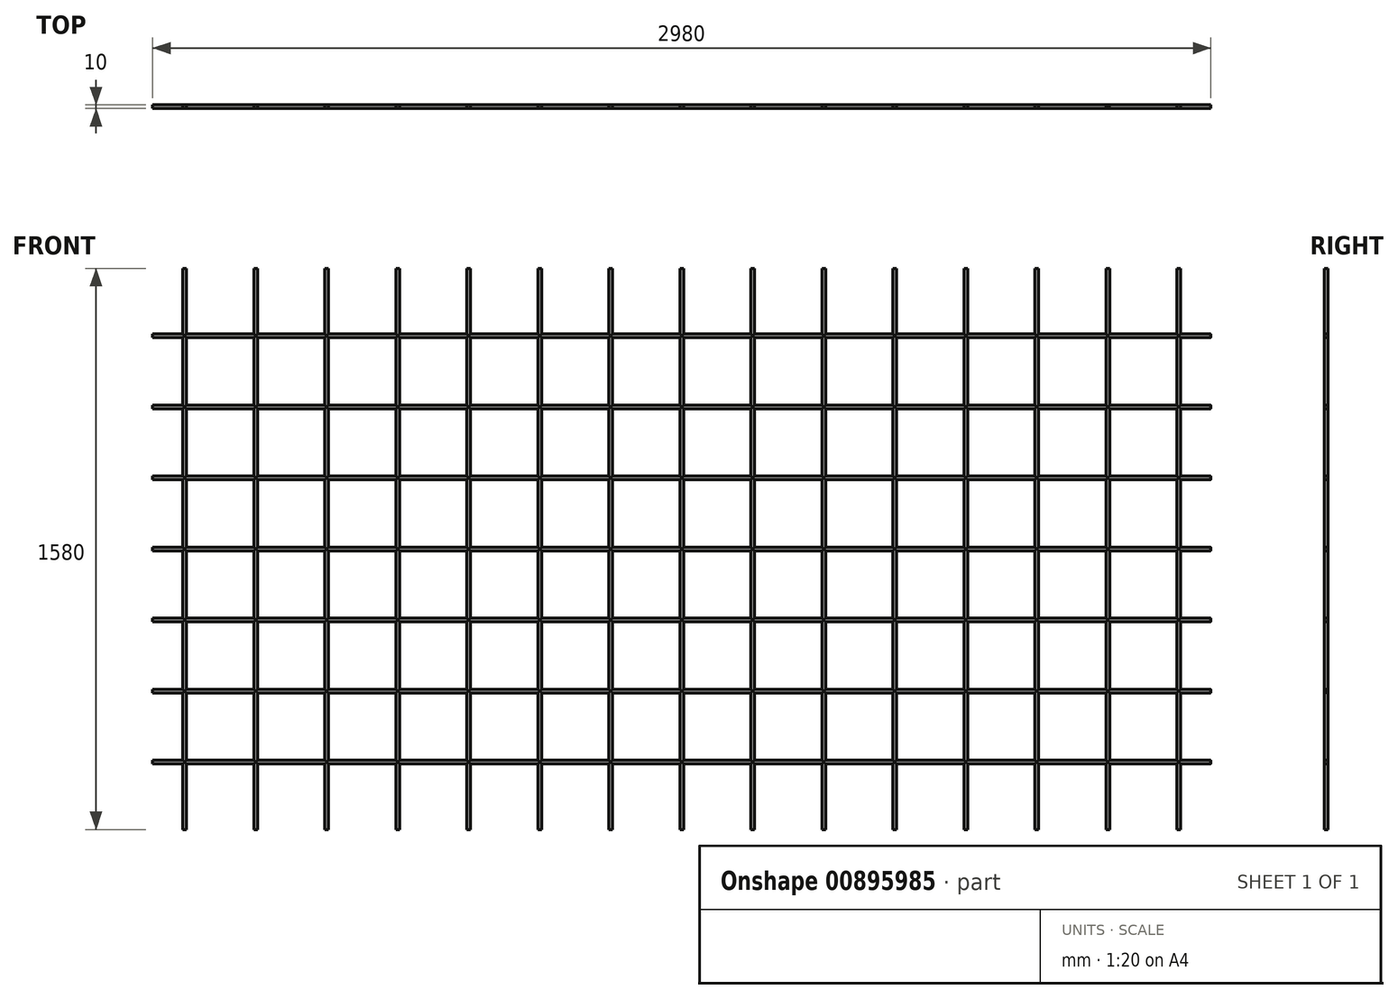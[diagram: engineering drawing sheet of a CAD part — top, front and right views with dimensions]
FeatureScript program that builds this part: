
annotation { "Feature Type Name" : "Feature", "Feature Type Description" : "" }
export const myFeature = defineFeature(function(context is Context, id is Id, definition is map)
    precondition{}
    {
        {
            var Q0;
            Q0=qCreatedBy(makeId("Front.planeOp"),FACE);
            var sketch = newSketch(context, id + "F0", { "sketchPlane" : qUnion([Q0])});
            skLineSegment(sketch, "E0", {"start": v(0, 0) * mm, "end": v(0, 1580) * mm});
            skLineSegment(sketch, "E1", {"start": v(0, 590) * mm, "end": v(-1490, 590) * mm});
            skLineSegment(sketch, "E2", {"start": v(0, 1190) * mm, "end": v(-1490, 1190) * mm});
            skLineSegment(sketch, "E3", {"start": v(0, 790) * mm, "end": v(-1490, 790) * mm});
            skLineSegment(sketch, "E4", {"start": v(0, 990) * mm, "end": v(-1490, 990) * mm});
            skLineSegment(sketch, "E5", {"start": v(-200, 1580) * mm, "end": v(-200, 0) * mm});
            skLineSegment(sketch, "E6", {"start": v(-400, 1580) * mm, "end": v(-400, 0) * mm});
            skLineSegment(sketch, "E7", {"start": v(0, 1390) * mm, "end": v(-1490, 1390) * mm});
            skLineSegment(sketch, "E8", {"start": v(0, 390) * mm, "end": v(-1490, 390) * mm});
            skLineSegment(sketch, "E9", {"start": v(0, 190) * mm, "end": v(-1490, 190) * mm});
            skLineSegment(sketch, "E10", {"start": v(-600, 1580) * mm, "end": v(-600, 0) * mm});
            skLineSegment(sketch, "E11", {"start": v(-800, 0) * mm, "end": v(-800, 1580) * mm});
            skLineSegment(sketch, "E12", {"start": v(-1000, 1580) * mm, "end": v(-1000, 0) * mm});
            skLineSegment(sketch, "E13", {"start": v(-1200, 0) * mm, "end": v(-1200, 1580) * mm});
            skLineSegment(sketch, "E14", {"start": v(-1400, 1580) * mm, "end": v(-1400, 0) * mm});
            skSolve(sketch);
        }
        {
            var Q0;
            Q0=qCreatedBy(makeId("Top.planeOp"),FACE);
            var sketch = newSketch(context, id + "F1", { "sketchPlane" : qUnion([Q0])});
            skCircle(sketch, "E15", {"center": v(-1400, 0) * mm, "radius": 5 * mm});
            skCircle(sketch, "E16", {"center": v(-1200, 0) * mm, "radius": 5 * mm});
            skCircle(sketch, "E17", {"center": v(-1000, 0) * mm, "radius": 5 * mm});
            skCircle(sketch, "E18", {"center": v(-800, 0) * mm, "radius": 5 * mm});
            skCircle(sketch, "E19", {"center": v(-600, 0) * mm, "radius": 5 * mm});
            skCircle(sketch, "E20", {"center": v(-400, 0) * mm, "radius": 5 * mm});
            skCircle(sketch, "E21", {"center": v(-200, 0) * mm, "radius": 5 * mm});
            skCircle(sketch, "E22", {"center": v(0, 0) * mm, "radius": 5 * mm});
            skSolve(sketch);
        }
        {
            var Q0;
            Q0=qCreatedBy(makeId("Right.planeOp"),FACE);
            var sketch = newSketch(context, id + "F2", { "sketchPlane" : qUnion([Q0])});
            skCircle(sketch, "E23", {"center": v(0, 190) * mm, "radius": 5 * mm});
            skCircle(sketch, "E24.0.1.0", {"center": v(0, 390) * mm, "radius": 5 * mm});
            skCircle(sketch, "E24.0.2.0", {"center": v(0, 590) * mm, "radius": 5 * mm});
            skCircle(sketch, "E24.0.3.0", {"center": v(0, 790) * mm, "radius": 5 * mm});
            skCircle(sketch, "E24.0.4.0", {"center": v(0, 990) * mm, "radius": 5 * mm});
            skCircle(sketch, "E24.0.5.0", {"center": v(0, 1190) * mm, "radius": 5 * mm});
            skCircle(sketch, "E24.0.6.0", {"center": v(0, 1390) * mm, "radius": 5 * mm});
            skLineSegment(sketch, "E24.direction1", {"start": v(0, 190) * mm, "end": v(25, 190) * mm, "construction": true});
            skLineSegment(sketch, "E24.direction2", {"start": v(0, 190) * mm, "end": v(0, 390) * mm, "construction": true});
            skSolve(sketch);
        }
        {
            var Q0;
            Q0=makeQuery(id+"F1.imprint","IMPRINT",FACE,{"disambiguationData":[TD([[makeQuery(id+"F1.imprint","IMPRINT",EDGE,{"derivedFrom":sQuery(id+"F1.wireOp",EDGE,"E22")}),1.0]])]});
            var Q1;
            Q1=makeQuery(id+"F1.imprint","IMPRINT",FACE,{"disambiguationData":[TD([[makeQuery(id+"F1.imprint","IMPRINT",EDGE,{"derivedFrom":sQuery(id+"F1.wireOp",EDGE,"E21")}),1.0]])]});
            var Q2;
            Q2=makeQuery(id+"F1.imprint","IMPRINT",FACE,{"disambiguationData":[TD([[makeQuery(id+"F1.imprint","IMPRINT",EDGE,{"derivedFrom":sQuery(id+"F1.wireOp",EDGE,"E20")}),1.0]])]});
            var Q3;
            Q3=makeQuery(id+"F1.imprint","IMPRINT",FACE,{"disambiguationData":[TD([[makeQuery(id+"F1.imprint","IMPRINT",EDGE,{"derivedFrom":sQuery(id+"F1.wireOp",EDGE,"E19")}),1.0]])]});
            var Q4;
            Q4=makeQuery(id+"F1.imprint","IMPRINT",FACE,{"disambiguationData":[TD([[makeQuery(id+"F1.imprint","IMPRINT",EDGE,{"derivedFrom":sQuery(id+"F1.wireOp",EDGE,"E18")}),1.0]])]});
            var Q5;
            Q5=makeQuery(id+"F1.imprint","IMPRINT",FACE,{"disambiguationData":[TD([[makeQuery(id+"F1.imprint","IMPRINT",EDGE,{"derivedFrom":sQuery(id+"F1.wireOp",EDGE,"E17")}),1.0]])]});
            var Q6;
            Q6=makeQuery(id+"F1.imprint","IMPRINT",FACE,{"disambiguationData":[TD([[makeQuery(id+"F1.imprint","IMPRINT",EDGE,{"derivedFrom":sQuery(id+"F1.wireOp",EDGE,"E16")}),1.0]])]});
            var Q7;
            Q7=makeQuery(id+"F1.imprint","IMPRINT",FACE,{"disambiguationData":[TD([[makeQuery(id+"F1.imprint","IMPRINT",EDGE,{"derivedFrom":sQuery(id+"F1.wireOp",EDGE,"E15")}),1.0]])]});
            var Q8;
            Q8=sQuery(id+"F0.wireOp",EDGE,"E14");
            sweep(context, id + "F3", {"profiles" : qUnion([Q0, Q1, Q2, Q3, Q4, Q5, Q6, Q7]), "path" : qUnion([Q8])});
        }
        {
            var Q0;
            Q0 = qSketchRegion(id + "F2", true);
            var Q1;
            Q1=sQuery(id+"F0.wireOp",EDGE,"E1");
            sweep(context, id + "F4", {"operationType" : NewBodyOperationType.ADD, "profiles" : qUnion([Q0]), "path" : qUnion([Q1])});
        }
        {
            var Q0;
            Q0=makeQuery(id+"F3.opSweep","SWEPT_BODY",BODY,{"disambiguationData":[OSD([sQuery(id+"F0.wireOp",EDGE,"E14"),sQuery(id+"F1.wireOp",EDGE,"E15")])]});
            var Q1;
            Q1=qCreatedBy(makeId("Right.planeOp"),FACE);
            mirror(context, id + "F5", {"operationType" : NewBodyOperationType.ADD, "entities" : qUnion([Q0]), "mirrorPlane" : qUnion([Q1])});
        }
    });
